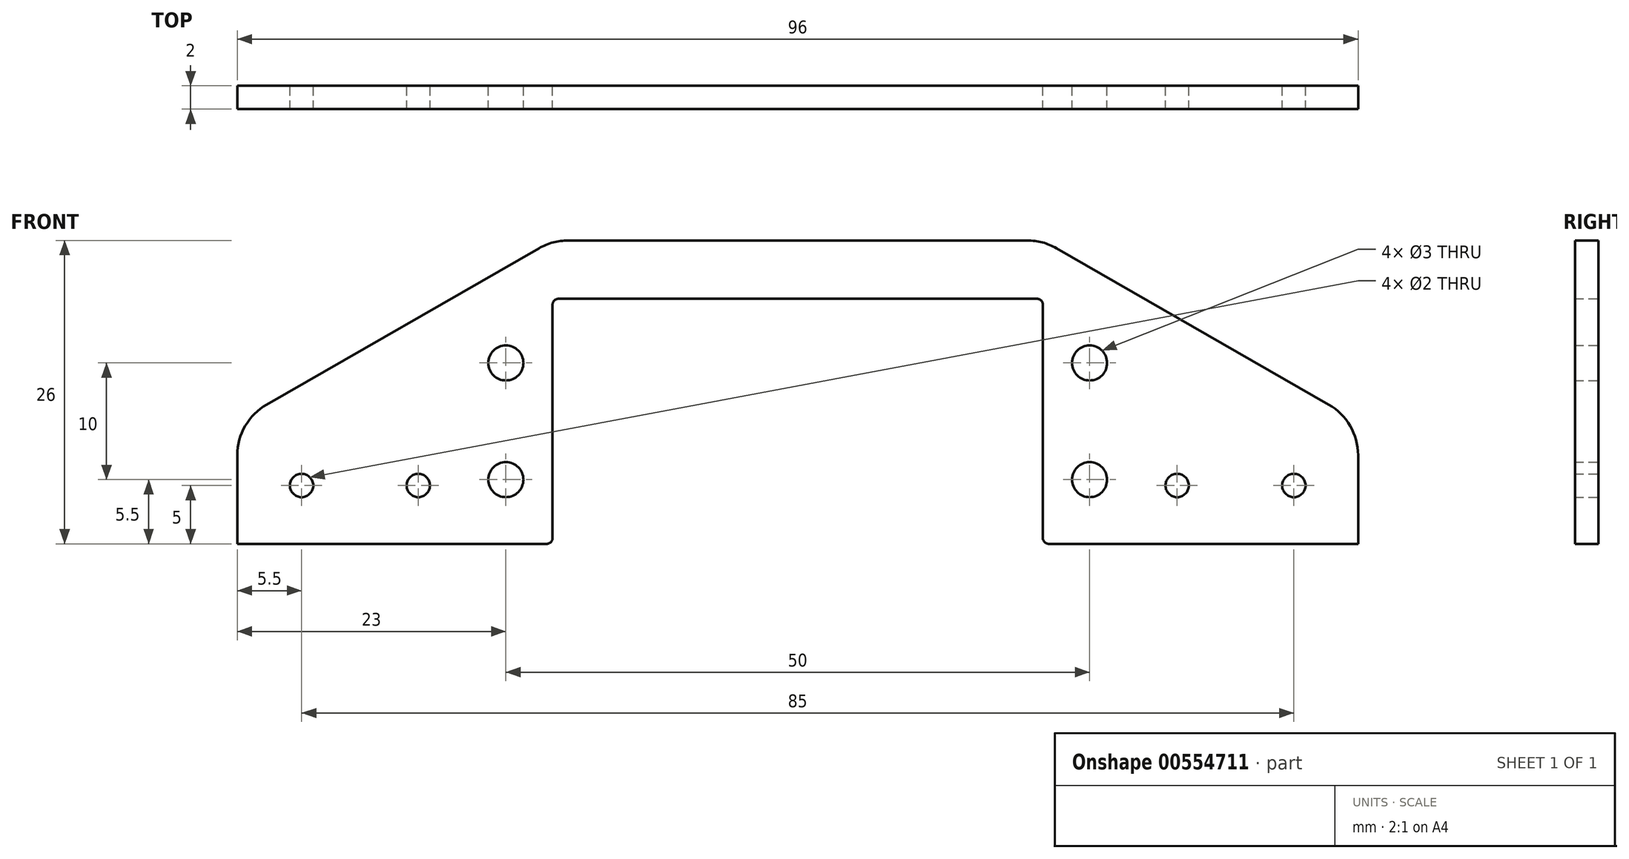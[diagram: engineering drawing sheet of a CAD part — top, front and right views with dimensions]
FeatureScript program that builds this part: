
annotation { "Feature Type Name" : "Feature", "Feature Type Description" : "" }
export const myFeature = defineFeature(function(context is Context, id is Id, definition is map)
    precondition{}
    {
        {
            var Q0;
            Q0=qCreatedBy(makeId("Front.planeOp"),FACE);
            var sketch = newSketch(context, id + "F0", { "sketchPlane" : qUnion([Q0])});
            skLineSegment(sketch, "E0.bottom", {"start": v(-20.5, 10.5) * mm, "end": v(20.5, 10.5) * mm});
            skLineSegment(sketch, "E0.left", {"start": v(-21, 10) * mm, "end": v(-21, -10) * mm});
            skLineSegment(sketch, "E0.right", {"start": v(21, 10) * mm, "end": v(21, -10) * mm});
            skPoint(sketch, "E0.middle", {"position": v(0, 0) * mm});
            skLineSegment(sketch, "E1.bottom", {"start": v(-25, 10.5) * mm, "end": v(25, 10.5) * mm, "construction": true});
            skLineSegment(sketch, "E1.top", {"start": v(-25, -10.5) * mm, "end": v(-21, -10.5) * mm, "construction": true});
            skLineSegment(sketch, "E1.left", {"start": v(-25, 10.5) * mm, "end": v(-25, -10.5) * mm, "construction": true});
            skLineSegment(sketch, "E1.right", {"start": v(25, 10.5) * mm, "end": v(25, -10.5) * mm, "construction": true});
            skLineSegment(sketch, "E2.bottom", {"start": v(-30.74, 5) * mm, "end": v(30.74, 5) * mm, "construction": true});
            skLineSegment(sketch, "E2.top", {"start": v(-30.74, -5) * mm, "end": v(30.74, -5) * mm, "construction": true});
            skLineSegment(sketch, "E2.left", {"start": v(-30.74, 5) * mm, "end": v(-30.74, -2.5) * mm, "construction": true});
            skLineSegment(sketch, "E2.right", {"start": v(30.74, 5) * mm, "end": v(30.74, -5) * mm, "construction": true});
            skLineSegment(sketch, "E3", {"start": v(-48, -10.5) * mm, "end": v(-21.5, -10.5) * mm});
            skLineSegment(sketch, "E4.bottom", {"start": v(-30, 17.05) * mm, "end": v(30, 17.05) * mm, "construction": true});
            skLineSegment(sketch, "E4.top", {"start": v(-30, -17.05) * mm, "end": v(30, -17.05) * mm, "construction": true});
            skLineSegment(sketch, "E4.left", {"start": v(-30, 17.05) * mm, "end": v(-30, -2.5) * mm, "construction": true});
            skLineSegment(sketch, "E4.right", {"start": v(30, 17.05) * mm, "end": v(30, -2.5) * mm, "construction": true});
            skPoint(sketch, "E5", {"position": v(-25, 5) * mm});
            skPoint(sketch, "E6", {"position": v(-25, -5) * mm});
            skPoint(sketch, "E7", {"position": v(25, 5) * mm});
            skPoint(sketch, "E8", {"position": v(25, -5) * mm});
            skCircle(sketch, "E9", {"center": v(25, 5) * mm, "radius": 1.5 * mm});
            skCircle(sketch, "E10", {"center": v(25, -5) * mm, "radius": 1.5 * mm});
            skCircle(sketch, "E11", {"center": v(-25, 5) * mm, "radius": 1.5 * mm});
            skCircle(sketch, "E12", {"center": v(-25, -5) * mm, "radius": 1.5 * mm});
            skLineSegment(sketch, "E13.bottom", {"start": v(30, -10.5) * mm, "end": v(45, -10.5) * mm});
            skLineSegment(sketch, "E13.top", {"start": v(30, -2.5) * mm, "end": v(30.74, -2.5) * mm});
            skLineSegment(sketch, "E13.left", {"start": v(30, -10.5) * mm, "end": v(30, -2.5) * mm});
            skPoint(sketch, "E14", {"position": v(32.5, -5.5) * mm});
            skPoint(sketch, "E15", {"position": v(42.5, -5.5) * mm});
            skCircle(sketch, "E16", {"center": v(32.5, -5.5) * mm, "radius": 1 * mm});
            skCircle(sketch, "E17", {"center": v(42.5, -5.5) * mm, "radius": 1 * mm});
            skLineSegment(sketch, "E18.bottom", {"start": v(-30, -10.5) * mm, "end": v(-45, -10.5) * mm});
            skLineSegment(sketch, "E18.top", {"start": v(-30, -2.5) * mm, "end": v(-30.74, -2.5) * mm});
            skLineSegment(sketch, "E18.left", {"start": v(-30, -5) * mm, "end": v(-30, -2.5) * mm});
            skPoint(sketch, "E19", {"position": v(-42.5, -5.5) * mm});
            skPoint(sketch, "E20", {"position": v(-32.5, -5.5) * mm});
            skCircle(sketch, "E21", {"center": v(-42.5, -5.5) * mm, "radius": 1 * mm});
            skCircle(sketch, "E22", {"center": v(-32.5, -5.5) * mm, "radius": 1 * mm});
            skPoint(sketch, "E23", {"position": v(-48, -10.5) * mm});
            skLineSegment(sketch, "E24", {"start": v(-48, -10.5) * mm, "end": v(-48, -2.9) * mm});
            skLineSegment(sketch, "E25", {"start": v(-45.49, 1.44) * mm, "end": v(-22.16, 14.84) * mm});
            skLineSegment(sketch, "E26", {"start": v(-19.67, 15.5) * mm, "end": v(0, 15.5) * mm});
            skPoint(sketch, "E27.visualSharp", {"position": v(-21, 15.5) * mm});
            skArc(sketch, "E27.filletArc", {"start": v(-19.67, 15.5) * mm, "mid": v(-20.95, 15.33) * mm, "end": v(-22.16, 14.84) * mm});
            skPoint(sketch, "E28.visualSharp", {"position": v(-48, 0) * mm});
            skArc(sketch, "E28.filletArc", {"start": v(-45.49, 1.44) * mm, "mid": v(-47.33, -0.39) * mm, "end": v(-48, -2.9) * mm});
            skLineSegment(sketch, "E29.MirrorCS", {"start": v(19.67, 15.5) * mm, "end": v(0, 15.5) * mm});
            skArc(sketch, "E30.MirrorCS", {"start": v(19.67, 15.5) * mm, "mid": v(20.95, 15.33) * mm, "end": v(22.16, 14.84) * mm});
            skLineSegment(sketch, "E31.MirrorCS", {"start": v(45.49, 1.44) * mm, "end": v(22.16, 14.84) * mm});
            skArc(sketch, "E32.MirrorCS", {"start": v(45.49, 1.44) * mm, "mid": v(47.33, -0.39) * mm, "end": v(48, -2.9) * mm});
            skLineSegment(sketch, "E33.MirrorCS", {"start": v(48, -10.5) * mm, "end": v(48, -2.9) * mm});
            skPoint(sketch, "E34.orphan", {"position": v(-81.64, -10.5) * mm});
            skLineSegment(sketch, "E35.trimOffspring", {"start": v(-30, -10.5) * mm, "end": v(-30, -17.05) * mm, "construction": true});
            skLineSegment(sketch, "E36.trimOffspring", {"start": v(30, -10.5) * mm, "end": v(30, -17.05) * mm, "construction": true});
            skLineSegment(sketch, "E37.trimOffspring", {"start": v(21, -10.5) * mm, "end": v(25, -10.5) * mm, "construction": true});
            skLineSegment(sketch, "E38.trimOffspring", {"start": v(21.5, -10.5) * mm, "end": v(85, -10.5) * mm});
            skPoint(sketch, "E39.visualSharp", {"position": v(-21, -10.5) * mm});
            skArc(sketch, "E39.filletArc", {"start": v(-21.5, -10.5) * mm, "mid": v(-21.15, -10.35) * mm, "end": v(-21, -10) * mm});
            skPoint(sketch, "E40.visualSharp", {"position": v(-21, 10.5) * mm});
            skArc(sketch, "E40.filletArc", {"start": v(-20.5, 10.5) * mm, "mid": v(-20.85, 10.35) * mm, "end": v(-21, 10) * mm});
            skPoint(sketch, "E41.visualSharp", {"position": v(21, 10.5) * mm});
            skArc(sketch, "E41.filletArc", {"start": v(21, 10) * mm, "mid": v(20.85, 10.35) * mm, "end": v(20.5, 10.5) * mm});
            skPoint(sketch, "E42.visualSharp", {"position": v(21, -10.5) * mm});
            skArc(sketch, "E42.filletArc", {"start": v(21, -10) * mm, "mid": v(21.15, -10.35) * mm, "end": v(21.5, -10.5) * mm});
            skSolve(sketch);
        }
        {
            var Q0;
            Q0=makeQuery(id+"F0.imprint","IMPRINT",FACE,{"disambiguationData":[TD([[makeQuery(id+"F0.imprint","IMPRINT",EDGE,{"derivedFrom":sQuery(id+"F0.wireOp",EDGE,"E0.bottom")}),1.0]])]});
            extrude(context, id + "F1", {"entities" : qUnion([Q0]), "depth" : 2 * mm, "offsetDistance" : 25 * mm});
        }
    });
